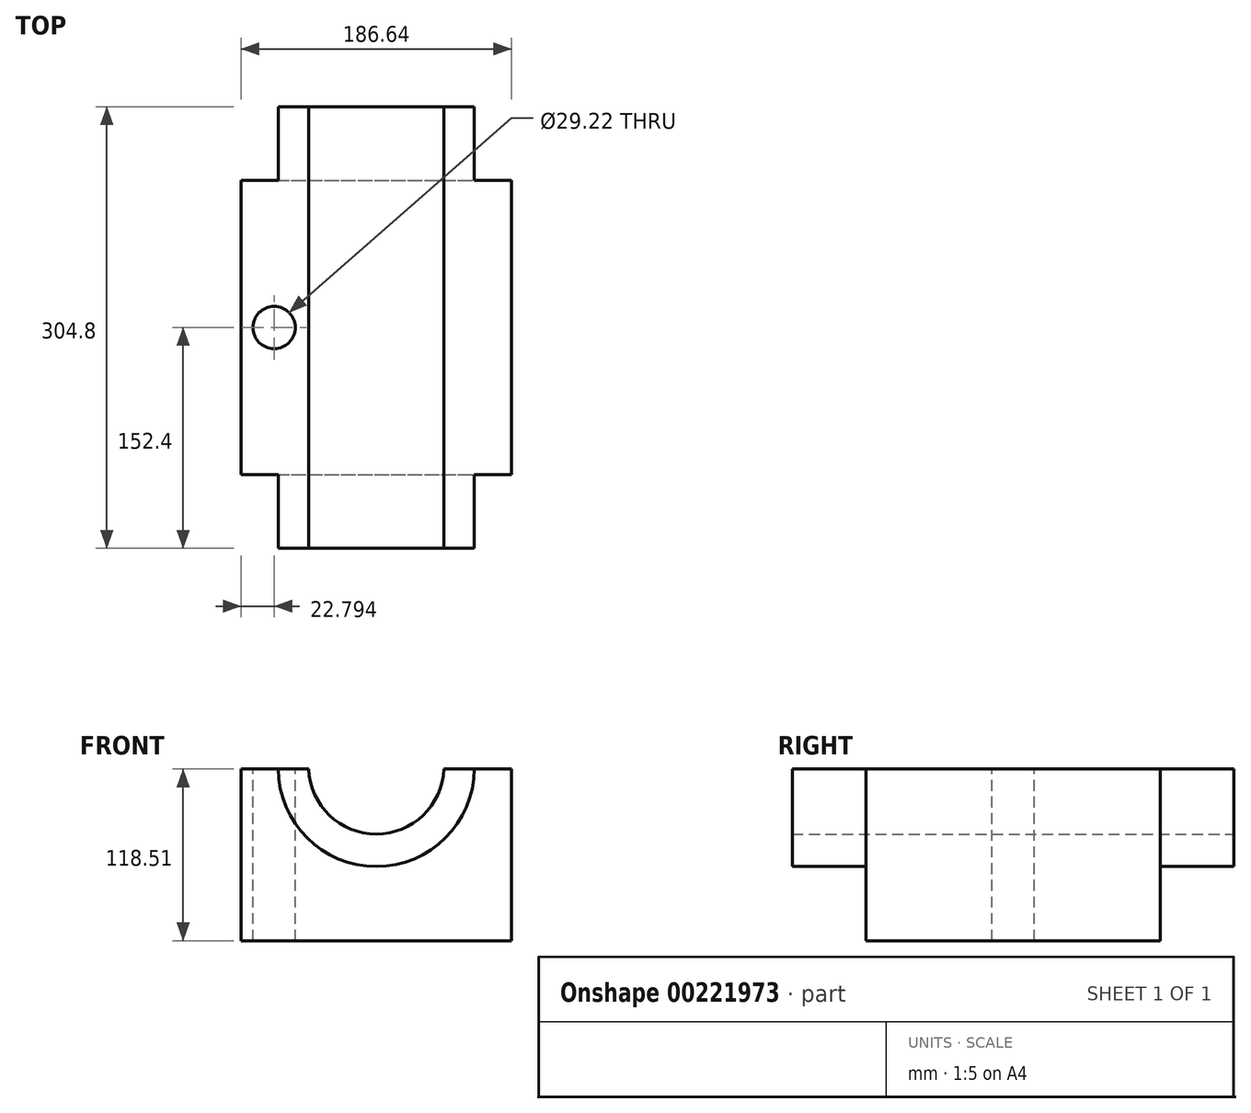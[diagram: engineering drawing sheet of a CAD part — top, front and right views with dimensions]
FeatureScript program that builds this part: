
annotation { "Feature Type Name" : "Feature", "Feature Type Description" : "" }
export const myFeature = defineFeature(function(context is Context, id is Id, definition is map)
    precondition{}
    {
        {
            var Q0;
            Q0=qCreatedBy(makeId("Front.planeOp"),FACE);
            var sketch = newSketch(context, id + "F0", { "sketchPlane" : qUnion([Q0])});
            skLineSegment(sketch, "E0", {"start": v(0, 0) * mm, "end": v(93.32, 0) * mm});
            skLineSegment(sketch, "E1", {"start": v(93.32, 0) * mm, "end": v(93.32, -118.5) * mm});
            skLineSegment(sketch, "E2", {"start": v(93.32, -118.5) * mm, "end": v(0, -118.5) * mm});
            skLineSegment(sketch, "E3.MirrorCS", {"start": v(0, 0) * mm, "end": v(-93.32, 0) * mm});
            skLineSegment(sketch, "E4.MirrorCS", {"start": v(-93.32, 0) * mm, "end": v(-93.32, -118.5) * mm});
            skLineSegment(sketch, "E5.MirrorCS", {"start": v(-93.32, -118.5) * mm, "end": v(0, -118.5) * mm});
            skArc(sketch, "E6", {"start": v(-46.66, 0) * mm, "mid": v(0, -44.85) * mm, "end": v(46.66, 0) * mm});
            skArc(sketch, "E7", {"start": v(-67.65, 0) * mm, "mid": v(0, -67.28) * mm, "end": v(67.65, 0) * mm});
            skLineSegment(sketch, "E8", {"start": v(-67.65, 0) * mm, "end": v(-46.66, 0) * mm});
            skLineSegment(sketch, "E9", {"start": v(46.66, 0) * mm, "end": v(67.65, 0) * mm});
            skSolve(sketch);
        }
        {
            var Q0;
            Q0=makeQuery(id+"F0.imprint","IMPRINT",FACE,{"disambiguationData":[TD([[makeQuery(id+"F0.imprint","IMPRINT",EDGE,{"derivedFrom":sQuery(id+"F0.wireOp",EDGE,"E6")}),-1.0]])]});
            extrude(context, id + "F1", {"entities" : qUnion([Q0]), "endBound" : BoundingType.SYMMETRIC, "depth" : 304.8 * mm});
        }
        {
            var Q0;
            {var subQ3=sQuery(id+"F0.wireOp",EDGE,"E1");Q0=makeQuery(id+"F0.imprint","IMPRINT",FACE,{"disambiguationData":[TD([[makeQuery(id+"F0.imprint","IMPRINT",EDGE,{"derivedFrom":subQ3}),-1.0]])]});}
            extrude(context, id + "F2", {"entities" : qUnion([Q0]), "operationType" : NewBodyOperationType.ADD, "endBound" : BoundingType.SYMMETRIC, "depth" : 203.2 * mm});
        }
        {
            var Q0;
            Q0=qCreatedBy(makeId("Top.planeOp"),FACE);
            var sketch = newSketch(context, id + "F3", { "sketchPlane" : qUnion([Q0])});
            skCircle(sketch, "E10", {"center": v(-70.53, 0) * mm, "radius": 14.61 * mm});
            skCircle(sketch, "E11.MirrorC", {"center": v(70.53, 0) * mm, "radius": 14.61 * mm});
            skSolve(sketch);
        }
        {
            var Q0;
            Q0=makeQuery(id+"F3.imprint","IMPRINT",FACE,{"disambiguationData":[TD([[makeQuery(id+"F3.imprint","IMPRINT",EDGE,{"derivedFrom":sQuery(id+"F3.wireOp",EDGE,"E10")}),1.0]])]});
            var Q1;
            Q1=makeQuery(id+"F3.imprint","IMPRINT",FACE,{"disambiguationData":[TD([[makeQuery(id+"F3.imprint","IMPRINT",EDGE,{"derivedFrom":sQuery(id+"F3.wireOp",EDGE,"E11.MirrorC")}),-1.0]])]});
            extrude(context, id + "F4", {"entities" : qUnion([Q0, Q1]), "operationType" : NewBodyOperationType.REMOVE, "oppositeDirection" : true, "depth" : 161.29 * mm});
        }
    });
